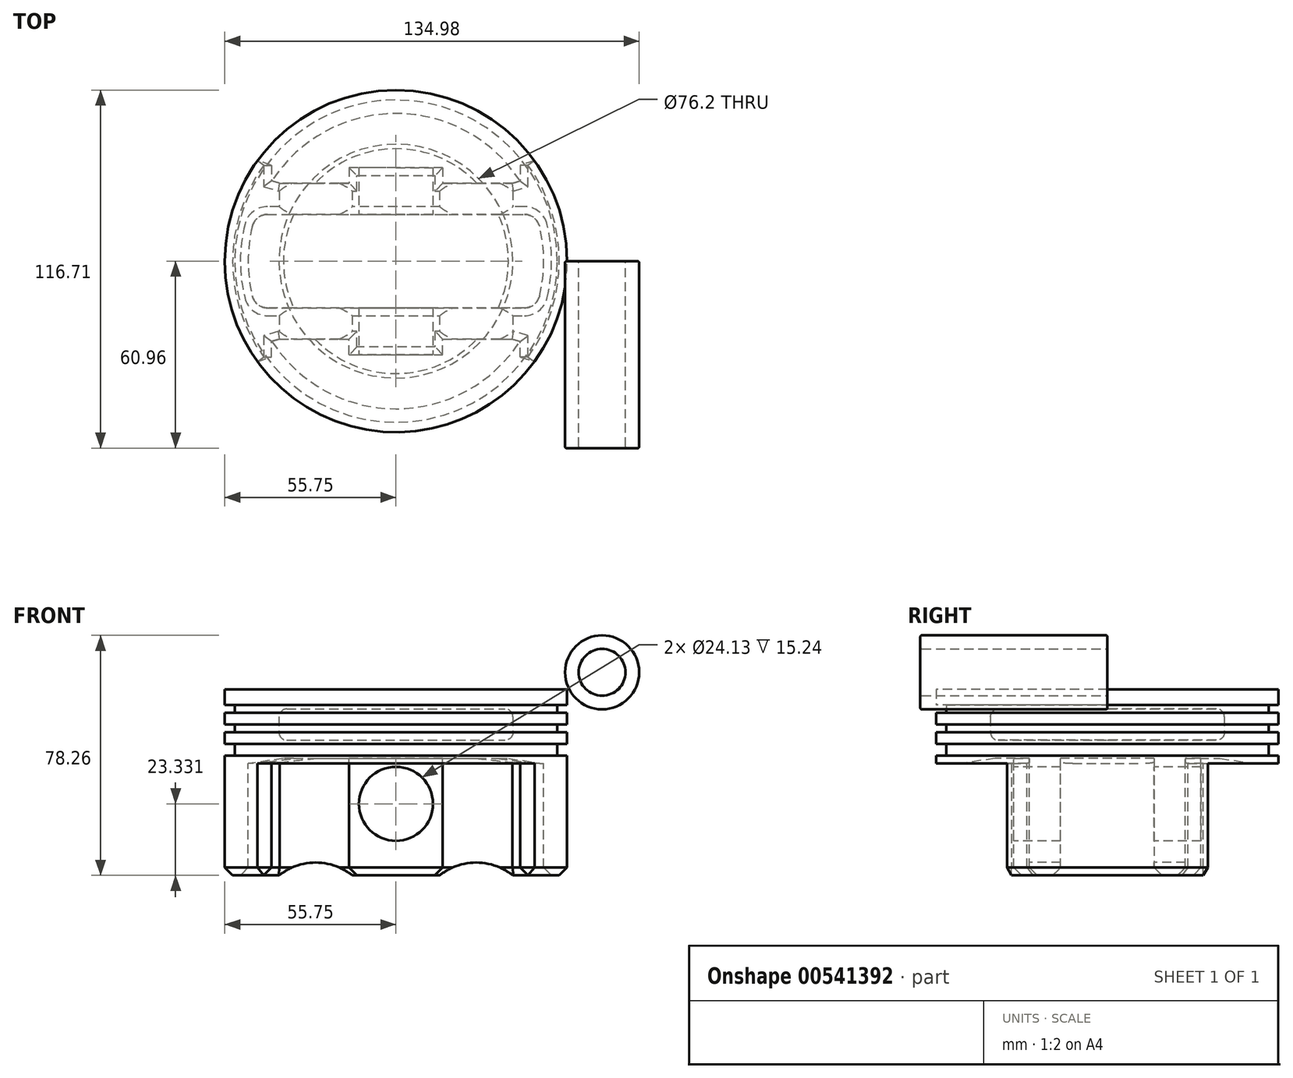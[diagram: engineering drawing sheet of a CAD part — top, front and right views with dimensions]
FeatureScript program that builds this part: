
annotation { "Feature Type Name" : "Feature", "Feature Type Description" : "" }
export const myFeature = defineFeature(function(context is Context, id is Id, definition is map)
    precondition{}
    {
        {
            var Q0;
            Q0=qCreatedBy(makeId("Front.planeOp"),FACE);
            var sketch = newSketch(context, id + "F0", { "sketchPlane" : qUnion([Q0])});
            skLineSegment(sketch, "E0", {"start": v(0, 51.93) * mm, "end": v(-55.75, 51.93) * mm});
            skLineSegment(sketch, "E1", {"start": v(-55.75, 51.93) * mm, "end": v(-55.75, 46.85) * mm});
            skLineSegment(sketch, "E2", {"start": v(-55.75, 46.85) * mm, "end": v(-52.54, 46.85) * mm});
            skLineSegment(sketch, "E3", {"start": v(-52.54, 46.85) * mm, "end": v(-52.54, 44.3) * mm});
            skLineSegment(sketch, "E4", {"start": v(-52.54, 44.3) * mm, "end": v(-55.75, 44.3) * mm});
            skLineSegment(sketch, "E5", {"start": v(-55.75, 44.3) * mm, "end": v(-55.75, 40.5) * mm});
            skLineSegment(sketch, "E6", {"start": v(-55.75, 40.5) * mm, "end": v(-52.54, 40.5) * mm});
            skLineSegment(sketch, "E7", {"start": v(-52.54, 40.5) * mm, "end": v(-52.54, 37.96) * mm});
            skLineSegment(sketch, "E8", {"start": v(-52.54, 37.96) * mm, "end": v(-55.75, 37.96) * mm});
            skLineSegment(sketch, "E9", {"start": v(-55.75, 37.96) * mm, "end": v(-55.75, 34.15) * mm});
            skLineSegment(sketch, "E10", {"start": v(-55.75, 34.15) * mm, "end": v(-52.54, 34.15) * mm});
            skLineSegment(sketch, "E11", {"start": v(-52.54, 34.15) * mm, "end": v(-52.54, 30.34) * mm});
            skLineSegment(sketch, "E12", {"start": v(-52.54, 30.34) * mm, "end": v(-55.75, 30.34) * mm});
            skLineSegment(sketch, "E13", {"start": v(-55.75, 30.34) * mm, "end": v(-55.75, -14.11) * mm});
            skPoint(sketch, "E14", {"position": v(0, 7.32) * mm});
            skCircle(sketch, "E15", {"center": v(0, 7.32) * mm, "radius": 12.07 * mm, "construction": true});
            skLineSegment(sketch, "E16", {"start": v(-55.75, -14.11) * mm, "end": v(-48.13, -14.11) * mm});
            skLineSegment(sketch, "E17", {"start": v(-48.13, -14.11) * mm, "end": v(-48.13, 27.8) * mm});
            skLineSegment(sketch, "E18", {"start": v(0, 45.58) * mm, "end": v(0, 51.93) * mm});
            skLineSegment(sketch, "E19", {"start": v(0, 45.58) * mm, "end": v(-29.96, 45.58) * mm});
            skLineSegment(sketch, "E20", {"start": v(-48.13, 27.8) * mm, "end": v(-36.63, 29.43) * mm});
            skLineSegment(sketch, "E21", {"start": v(-36.63, 29.43) * mm, "end": v(0, 29.43) * mm});
            skLineSegment(sketch, "E22", {"start": v(-29.96, 45.58) * mm, "end": v(-35.56, 45.58) * mm});
            skLineSegment(sketch, "E23", {"start": v(-38.1, 43.04) * mm, "end": v(-38.1, 37.96) * mm});
            skLineSegment(sketch, "E24", {"start": v(-35.56, 35.42) * mm, "end": v(0, 35.42) * mm});
            skPoint(sketch, "E25.visualSharp", {"position": v(-38.1, 45.58) * mm});
            skArc(sketch, "E25.filletArc", {"start": v(-35.56, 45.58) * mm, "mid": v(-37.36, 44.83) * mm, "end": v(-38.1, 43.04) * mm});
            skPoint(sketch, "E26.visualSharp", {"position": v(-38.1, 35.42) * mm});
            skArc(sketch, "E26.filletArc", {"start": v(-38.1, 37.96) * mm, "mid": v(-37.36, 36.16) * mm, "end": v(-35.56, 35.42) * mm});
            skLineSegment(sketch, "E27", {"start": v(0, 35.42) * mm, "end": v(0, 29.43) * mm});
            skLineSegment(sketch, "E28", {"start": v(-48.13, 27.8) * mm, "end": v(-55.75, 27.8) * mm});
            skSolve(sketch);
        }
        {
            var Q0;
            Q0=makeQuery(id+"F0.imprint","IMPRINT",FACE,{"disambiguationData":[TD([[makeQuery(id+"F0.imprint","IMPRINT",EDGE,{"derivedFrom":sQuery(id+"F0.wireOp",EDGE,"E0")}),1.0]])]});
            var Q1;
            Q1=sQuery(id+"F0.wireOp",EDGE,"E18");
            revolve(context, id + "F1", {"entities" : qUnion([Q0]), "axis" : qUnion([Q1]), "revolveType" : RevolveType.FULL});
        }
        {
            var Q0;
            Q0=makeQuery(id+"F1.opRevolve","SWEPT_FACE",FACE,{"disambiguationData":[OSD([sQuery(id+"F0.wireOp",EDGE,"E21")])]});
            var sketch = newSketch(context, id + "F2", { "sketchPlane" : qUnion([Q0])});
            skArc(sketch, "E29", {"start": v(-40.53, 38.29) * mm, "mid": v(-55.2, 7.89) * mm, "end": v(-49.63, -25.4) * mm});
            skLineSegment(sketch, "E30", {"start": v(-37.92, 25.4) * mm, "end": v(-15.24, 25.4) * mm});
            skLineSegment(sketch, "E31.MirrorCS", {"start": v(-37.92, -25.4) * mm, "end": v(-15.24, -25.4) * mm});
            skArc(sketch, "E32.trimOffspring", {"start": v(49.63, -25.4) * mm, "mid": v(55.75, 0) * mm, "end": v(49.63, 25.4) * mm});
            skLineSegment(sketch, "E33", {"start": v(-45.66, 15.24) * mm, "end": v(0, 15.24) * mm});
            skLineSegment(sketch, "E34.MirrorCS", {"start": v(-45.66, -15.24) * mm, "end": v(0, -15.24) * mm});
            skLineSegment(sketch, "E35.MirrorCS", {"start": v(45.66, 15.24) * mm, "end": v(0, 15.24) * mm});
            skLineSegment(sketch, "E36.MirrorCS", {"start": v(45.66, -15.24) * mm, "end": v(0, -15.24) * mm});
            skLineSegment(sketch, "E37", {"start": v(-37.92, 25.4) * mm, "end": v(-40.53, 26.18) * mm});
            skLineSegment(sketch, "E38", {"start": v(-40.53, 26.18) * mm, "end": v(-40.53, 38.29) * mm});
            skPoint(sketch, "E39.orphan", {"position": v(-49.63, 25.4) * mm});
            skLineSegment(sketch, "E40.MirrorCS", {"start": v(40.53, 26.18) * mm, "end": v(40.53, 38.29) * mm});
            skLineSegment(sketch, "E41.MirrorCS", {"start": v(37.92, 25.4) * mm, "end": v(40.53, 26.18) * mm});
            skArc(sketch, "E42.MirrorCS", {"start": v(40.53, 38.29) * mm, "mid": v(55.2, 7.89) * mm, "end": v(49.63, -25.4) * mm});
            skLineSegment(sketch, "E43.MirrorCS", {"start": v(-40.53, -26.18) * mm, "end": v(-40.53, -38.29) * mm});
            skLineSegment(sketch, "E44.MirrorCS", {"start": v(-37.92, -25.4) * mm, "end": v(-40.53, -26.18) * mm});
            skArc(sketch, "E45.MirrorCS", {"start": v(-40.53, -38.29) * mm, "mid": v(-55.2, -7.89) * mm, "end": v(-49.63, 25.4) * mm});
            skArc(sketch, "E46.MirrorCS", {"start": v(40.53, -38.29) * mm, "mid": v(55.2, -7.89) * mm, "end": v(49.63, 25.4) * mm});
            skLineSegment(sketch, "E47.MirrorCS", {"start": v(40.53, -26.18) * mm, "end": v(40.53, -38.29) * mm});
            skLineSegment(sketch, "E48.MirrorCS", {"start": v(37.92, -25.4) * mm, "end": v(40.53, -26.18) * mm});
            skArc(sketch, "E49", {"start": v(40.41, -26.14) * mm, "mid": v(48.13, 0) * mm, "end": v(40.41, 26.14) * mm});
            skPoint(sketch, "E50.orphan", {"position": v(-25.4, 15.24) * mm});
            skPoint(sketch, "E51.orphan", {"position": v(-25.4, -15.24) * mm});
            skPoint(sketch, "E52.orphan", {"position": v(25.4, -15.24) * mm});
            skPoint(sketch, "E53.orphan", {"position": v(25.4, 15.24) * mm});
            skArc(sketch, "E54.trimOffspring", {"start": v(-40.41, 26.14) * mm, "mid": v(-48.13, 0) * mm, "end": v(-40.41, -26.14) * mm});
            skLineSegment(sketch, "E55", {"start": v(0, 30.48) * mm, "end": v(-15.24, 30.48) * mm});
            skPoint(sketch, "E55.startSnap0", {"position": v(0, 25.4) * mm});
            skLineSegment(sketch, "E56", {"start": v(-15.24, 30.48) * mm, "end": v(-15.24, 25.4) * mm});
            skLineSegment(sketch, "E57.MirrorCS", {"start": v(15.24, 30.48) * mm, "end": v(15.24, 25.4) * mm});
            skLineSegment(sketch, "E58.MirrorCS", {"start": v(0, 30.48) * mm, "end": v(15.24, 30.48) * mm});
            skLineSegment(sketch, "E59.trimOffspring", {"start": v(15.24, 25.4) * mm, "end": v(37.92, 25.4) * mm});
            skLineSegment(sketch, "E60.MirrorCS", {"start": v(-15.24, -30.48) * mm, "end": v(-15.24, -25.4) * mm});
            skLineSegment(sketch, "E61.MirrorCS", {"start": v(0, -30.48) * mm, "end": v(-15.24, -30.48) * mm});
            skLineSegment(sketch, "E62.MirrorCS", {"start": v(15.24, -30.48) * mm, "end": v(15.24, -25.4) * mm});
            skLineSegment(sketch, "E63.MirrorCS", {"start": v(0, -30.48) * mm, "end": v(15.24, -30.48) * mm});
            skLineSegment(sketch, "E64.trimOffspring", {"start": v(15.24, -25.4) * mm, "end": v(37.92, -25.4) * mm});
            skSolve(sketch);
        }
        {
            var Q0;
            Q0 = qSketchRegion(id + "F2", true);
            extrude(context, id + "F3", {"entities" : qUnion([Q0]), "operationType" : NewBodyOperationType.ADD, "depth" : 38.1 * mm, "offsetDistance" : 25.4 * mm});
        }
        {
            var Q0;
            Q0=makeQuery(id+"F3.opExtrude","SWEPT_FACE",FACE,{"disambiguationData":[OSD([sQuery(id+"F2.wireOp",EDGE,"E55"),sQuery(id+"F2.wireOp",EDGE,"E58.MirrorCS")])]});
            var sketch = newSketch(context, id + "F4", { "sketchPlane" : qUnion([Q0])});
            skPoint(sketch, "E65", {"position": v(0, 14.66) * mm});
            skCircle(sketch, "E66", {"center": v(0, 14.66) * mm, "radius": 12.07 * mm});
            skSolve(sketch);
        }
        {
            var Q0;
            Q0=makeQuery(id+"F4.imprint","IMPRINT",FACE,{"disambiguationData":[TD([[makeQuery(id+"F4.imprint","IMPRINT",EDGE,{"derivedFrom":sQuery(id+"F4.wireOp",EDGE,"E66")}),1.0]])]});
            extrude(context, id + "F5", {"entities" : qUnion([Q0]), "operationType" : NewBodyOperationType.REMOVE, "endBound" : BoundingType.SYMMETRIC, "oppositeDirection" : true, "depth" : 202.7 * mm, "offsetDistance" : 25.4 * mm});
        }
        {
            var Q0;
            Q0=makeQuery(id+"F3.opExtrude","SWEPT_EDGE",EDGE,{"disambiguationData":[OSD([sQuery(id+"F2.wireOp",EDGE,"E35.MirrorCS"),sQuery(id+"F2.wireOp",EDGE,"E49")])]});
            var Q1;
            Q1=makeQuery(id+"F3.opExtrude","SWEPT_EDGE",EDGE,{"disambiguationData":[OSD([sQuery(id+"F2.wireOp",EDGE,"E33"),sQuery(id+"F2.wireOp",EDGE,"E54.trimOffspring")])]});
            var Q2;
            Q2=makeQuery(id+"F3.opExtrude","SWEPT_EDGE",EDGE,{"disambiguationData":[OSD([sQuery(id+"F2.wireOp",EDGE,"E34.MirrorCS"),sQuery(id+"F2.wireOp",EDGE,"E54.trimOffspring")])]});
            var Q3;
            Q3=makeQuery(id+"F3.opExtrude","SWEPT_EDGE",EDGE,{"disambiguationData":[OSD([sQuery(id+"F2.wireOp",EDGE,"E36.MirrorCS"),sQuery(id+"F2.wireOp",EDGE,"E49")])]});
            fillet(context, id + "F6", {"entities" : qUnion([Q0, Q1, Q2, Q3]), "radius" : 5.08 * mm, "tangentPropagation" : true, "allowEdgeOverflow" : false});
        }
        {
            var Q0;
            Q0=makeQuery(id+"F3.opExtrude","SWEPT_EDGE",EDGE,{"disambiguationData":[OSD([sQuery(id+"F2.wireOp",EDGE,"E43.MirrorCS"),sQuery(id+"F2.wireOp",EDGE,"E45.MirrorCS")])]});
            var Q1;
            Q1=makeQuery(id+"F3.opExtrude","SWEPT_EDGE",EDGE,{"disambiguationData":[OSD([sQuery(id+"F2.wireOp",EDGE,"E46.MirrorCS"),sQuery(id+"F2.wireOp",EDGE,"E47.MirrorCS")])]});
            var Q2;
            Q2=makeQuery(id+"F3.opExtrude","SWEPT_EDGE",EDGE,{"disambiguationData":[OSD([sQuery(id+"F2.wireOp",EDGE,"E40.MirrorCS"),sQuery(id+"F2.wireOp",EDGE,"E42.MirrorCS")])]});
            var Q3;
            Q3=makeQuery(id+"F3.opExtrude","SWEPT_EDGE",EDGE,{"disambiguationData":[OSD([sQuery(id+"F2.wireOp",EDGE,"E29"),sQuery(id+"F2.wireOp",EDGE,"E38")])]});
            var Q4;
            Q4=makeQuery(id+"F3.opExtrude","CAP_FACE",FACE,{"disambiguationData":[OSD([sQuery(id+"F2.wireOp",EDGE,"E29"),sQuery(id+"F2.wireOp",EDGE,"E30"),sQuery(id+"F2.wireOp",EDGE,"E31.MirrorCS"),sQuery(id+"F2.wireOp",EDGE,"E33"),sQuery(id+"F2.wireOp",EDGE,"E34.MirrorCS"),sQuery(id+"F2.wireOp",EDGE,"E35.MirrorCS"),sQuery(id+"F2.wireOp",EDGE,"E36.MirrorCS"),sQuery(id+"F2.wireOp",EDGE,"E37"),sQuery(id+"F2.wireOp",EDGE,"E38"),sQuery(id+"F2.wireOp",EDGE,"E40.MirrorCS"),sQuery(id+"F2.wireOp",EDGE,"E41.MirrorCS"),sQuery(id+"F2.wireOp",EDGE,"E42.MirrorCS"),sQuery(id+"F2.wireOp",EDGE,"E43.MirrorCS"),sQuery(id+"F2.wireOp",EDGE,"E44.MirrorCS"),sQuery(id+"F2.wireOp",EDGE,"E45.MirrorCS"),sQuery(id+"F2.wireOp",EDGE,"E46.MirrorCS"),sQuery(id+"F2.wireOp",EDGE,"E47.MirrorCS"),sQuery(id+"F2.wireOp",EDGE,"E48.MirrorCS"),sQuery(id+"F2.wireOp",EDGE,"E49"),sQuery(id+"F2.wireOp",EDGE,"E54.trimOffspring"),sQuery(id+"F2.wireOp",EDGE,"E55"),sQuery(id+"F2.wireOp",EDGE,"E56"),sQuery(id+"F2.wireOp",EDGE,"E57.MirrorCS"),sQuery(id+"F2.wireOp",EDGE,"E58.MirrorCS"),sQuery(id+"F2.wireOp",EDGE,"E59.trimOffspring"),sQuery(id+"F2.wireOp",EDGE,"E60.MirrorCS"),sQuery(id+"F2.wireOp",EDGE,"E61.MirrorCS"),sQuery(id+"F2.wireOp",EDGE,"E62.MirrorCS"),sQuery(id+"F2.wireOp",EDGE,"E63.MirrorCS"),sQuery(id+"F2.wireOp",EDGE,"E64.trimOffspring")])],"isStart":false});
            chamfer(context, id + "F7", {"entities" : qUnion([Q0, Q1, Q2, Q3, Q4]), "width" : 2.54 * mm, "tangentPropagation" : true});
        }
        {
            var Q0;
            Q0=qCreatedBy(makeId("Front.planeOp"),FACE);
            var sketch = newSketch(context, id + "F8", { "sketchPlane" : qUnion([Q0])});
            skArc(sketch, "E67", {"start": v(-14.23, -8.67) * mm, "mid": v(-26.15, -4.5) * mm, "end": v(-38.07, -8.67) * mm});
            skArc(sketch, "E68.MirrorCS", {"start": v(14.23, -8.67) * mm, "mid": v(26.15, -4.5) * mm, "end": v(38.07, -8.67) * mm});
            skLineSegment(sketch, "E69", {"start": v(-38.07, -8.67) * mm, "end": v(-38.07, -24.55) * mm});
            skLineSegment(sketch, "E70", {"start": v(-38.07, -24.55) * mm, "end": v(41.3, -22.25) * mm});
            skLineSegment(sketch, "E71", {"start": v(41.3, -22.25) * mm, "end": v(38.07, -8.67) * mm});
            skLineSegment(sketch, "E72", {"start": v(-14.23, -8.67) * mm, "end": v(-14.23, -14.03) * mm});
            skLineSegment(sketch, "E73", {"start": v(-14.23, -14.03) * mm, "end": v(14.66, -14.03) * mm});
            skLineSegment(sketch, "E74", {"start": v(14.66, -14.03) * mm, "end": v(14.23, -8.67) * mm});
            skSolve(sketch);
        }
        {
            var Q0;
            Q0=makeQuery(id+"F8.imprint","IMPRINT",FACE,{"disambiguationData":[TD([[makeQuery(id+"F8.imprint","IMPRINT",EDGE,{"derivedFrom":sQuery(id+"F8.wireOp",EDGE,"E67")}),1.0]])]});
            extrude(context, id + "F9", {"entities" : qUnion([Q0]), "operationType" : NewBodyOperationType.REMOVE, "endBound" : BoundingType.SYMMETRIC, "oppositeDirection" : true, "depth" : 142.75 * mm, "offsetDistance" : 25.4 * mm});
        }
        {
            var Q0;
            Q0=qCreatedBy(makeId("Front.planeOp"),FACE);
            var sketch = newSketch(context, id + "F10", { "sketchPlane" : qUnion([Q0])});
            skCircle(sketch, "E75", {"center": v(67.16, 57.53) * mm, "radius": 12.07 * mm});
            skCircle(sketch, "E76", {"center": v(67.16, 57.53) * mm, "radius": 7.62 * mm});
            skSolve(sketch);
        }
        {
            var Q0;
            Q0=makeQuery(id+"F10.imprint","IMPRINT",FACE,{"disambiguationData":[TD([[makeQuery(id+"F10.imprint","IMPRINT",EDGE,{"derivedFrom":sQuery(id+"F10.wireOp",EDGE,"E75")}),1.0]])]});
            extrude(context, id + "F11", {"entities" : qUnion([Q0]), "depth" : 60.96 * mm, "offsetDistance" : 25.4 * mm});
        }
        {
            var Q0;
            Q0=makeQuery(id+"F11.opExtrude","CAP_EDGE",EDGE,{"disambiguationData":[OSD([sQuery(id+"F10.wireOp",EDGE,"E76")])],"isStart":true});
            var Q1;
            Q1=makeQuery(id+"F11.opExtrude","CAP_EDGE",EDGE,{"disambiguationData":[OSD([sQuery(id+"F10.wireOp",EDGE,"E75")])],"isStart":true});
            var Q2;
            Q2=makeQuery(id+"F11.opExtrude","CAP_FACE",FACE,{"disambiguationData":[OSD([sQuery(id+"F10.wireOp",EDGE,"E75"),sQuery(id+"F10.wireOp",EDGE,"E76")])],"isStart":false});
            fillet(context, id + "F12", {"entities" : qUnion([Q0, Q1, Q2]), "radius" : 0.5 * mm, "tangentPropagation" : true, "allowEdgeOverflow" : false});
        }
    });
